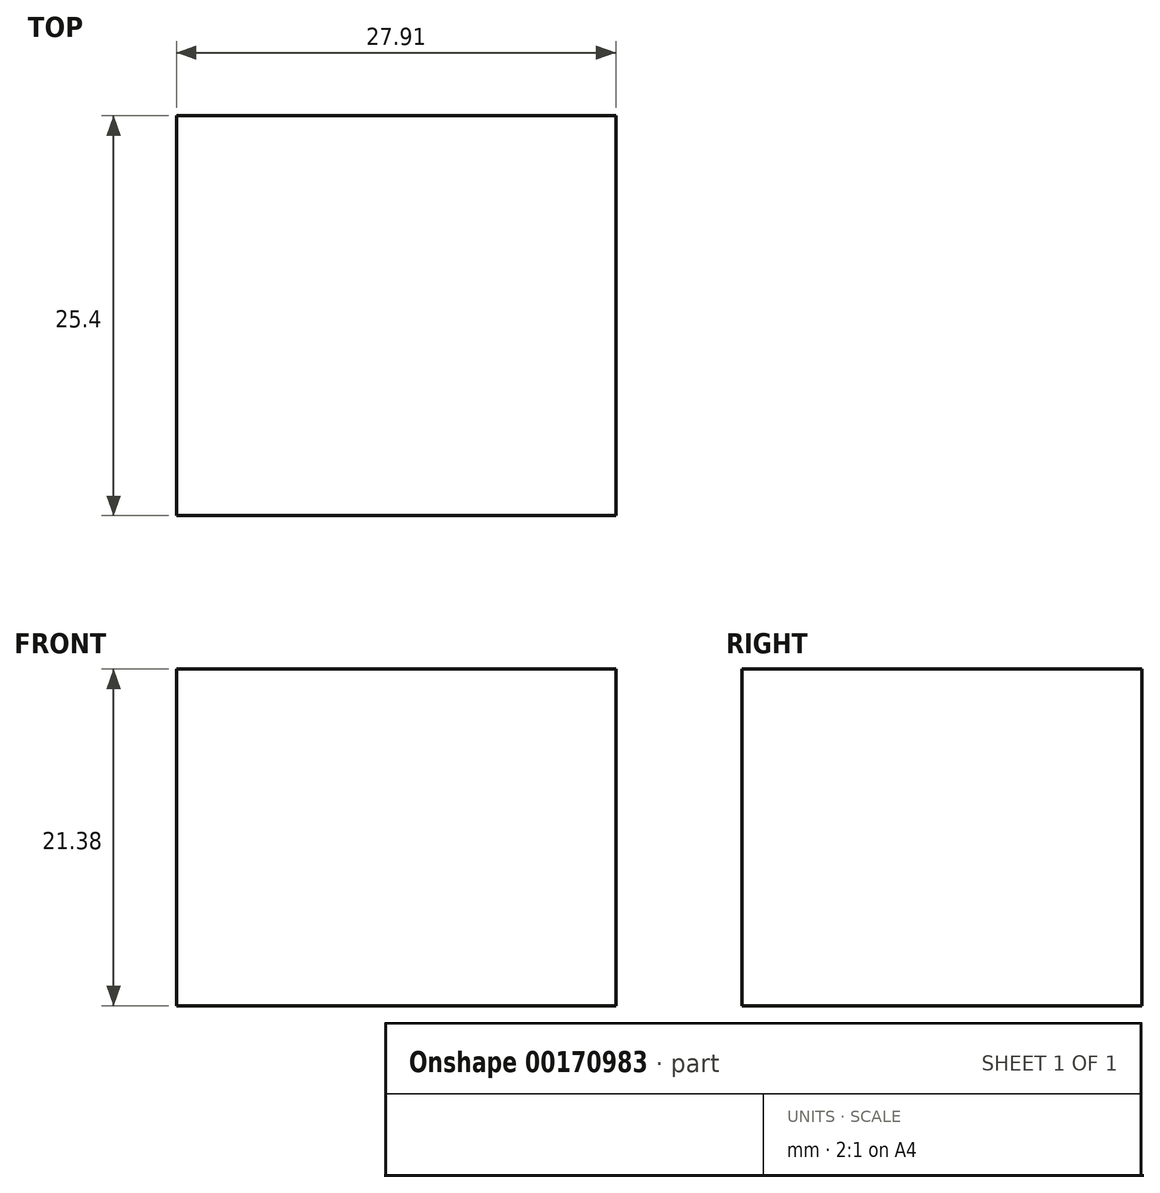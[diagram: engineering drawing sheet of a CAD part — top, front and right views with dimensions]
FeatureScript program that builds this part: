
annotation { "Feature Type Name" : "Feature", "Feature Type Description" : "" }
export const myFeature = defineFeature(function(context is Context, id is Id, definition is map)
    precondition{}
    {
        {
            var Q0;
            Q0=qCreatedBy(makeId("Front.planeOp"),FACE);
            var sketch = newSketch(context, id + "F0", { "sketchPlane" : qUnion([Q0])});
            skLineSegment(sketch, "E0.bottom", {"start": v(-17.76, 0) * mm, "end": v(10.15, 0) * mm});
            skLineSegment(sketch, "E0.top", {"start": v(-17.76, -21.38) * mm, "end": v(10.15, -21.38) * mm});
            skLineSegment(sketch, "E0.left", {"start": v(-17.76, 0) * mm, "end": v(-17.76, -21.38) * mm});
            skLineSegment(sketch, "E0.right", {"start": v(10.15, 0) * mm, "end": v(10.15, -21.38) * mm});
            skSolve(sketch);
        }
        {
            var Q0;
            Q0 = qSketchRegion(id + "F0", true);
            extrude(context, id + "F1", {"entities" : qUnion([Q0]), "depth" : 25.4 * mm});
        }
    });
